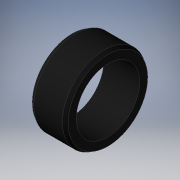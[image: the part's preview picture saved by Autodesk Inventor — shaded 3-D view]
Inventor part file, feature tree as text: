
AUTODESK INVENTOR PART (.ipt)
format: ipt  version: 2019 (Build 230136000, 136)  size: 130,560 bytes
history: native  units: mm
features: other x21, revolve x1, sketch x1
ambient origin geometry x8: Origin, YZ Plane, XZ Plane, XY Plane, X Axis, Y Axis, Z Axis, Center Point
bodies: Solid1 (feature_tree)
feature tree (23):
  revolve  "Revolution1"  [1 undecoded]
  other  "anbau_XY"
  other  "anbau_YZ"
  other  "anbau_ZX"
  other  "anbau_X"
  other  "anbau_Y"
  other  "anbau_Z"
  other  "anbau_Center"
  other  "insert_XY"
  other  "insert_YZ"
  other  "insert_ZX"
  other  "insert_X"
  other  "insert_Y"
  other  "insert_Z"
  other  "insert_Center"
  other  "schraube_punkt_XY"
  other  "schraube_punkt_YZ"
  other  "schraube_punkt_ZX"
  other  "schraube_punkt_X"
  other  "schraube_punkt_Y"
  other  "schraube_punkt_Z"
  other  "schraube_punkt_Center"
  sketch  "Sketch_1"  dims[d0=360.0deg d1=0.0mm d2=0.0mm d3=0.0mm]
note: 1 required parameter value undecoded (feature->parameter linkage not recoverable at this tier; creation-order binding heuristic only, values carry confidence <= 0.55)
